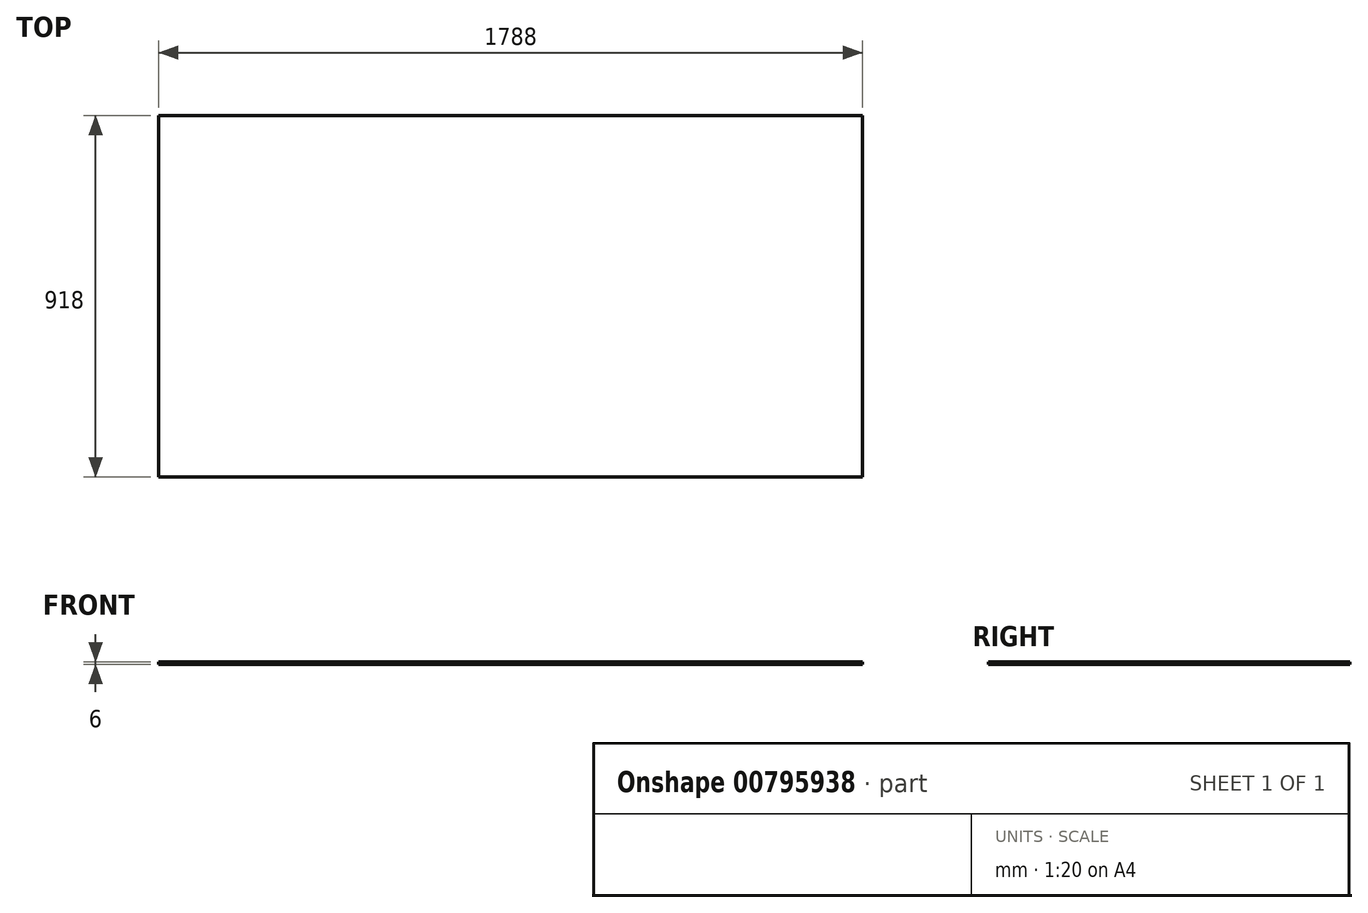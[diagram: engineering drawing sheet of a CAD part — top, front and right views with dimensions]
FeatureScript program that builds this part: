
annotation { "Feature Type Name" : "Feature", "Feature Type Description" : "" }
export const myFeature = defineFeature(function(context is Context, id is Id, definition is map)
    precondition{}
    {
        {
            var Q0;
            Q0=qCreatedBy(makeId("Top.planeOp"),FACE);
            var sketch = newSketch(context, id + "F0", { "sketchPlane" : qUnion([Q0])});
            skLineSegment(sketch, "E0.bottom", {"start": v(894, 459) * mm, "end": v(-894, 459) * mm});
            skLineSegment(sketch, "E0.top", {"start": v(894, -459) * mm, "end": v(-894, -459) * mm});
            skLineSegment(sketch, "E0.left", {"start": v(894, 459) * mm, "end": v(894, -459) * mm});
            skLineSegment(sketch, "E0.right", {"start": v(-894, 459) * mm, "end": v(-894, -459) * mm});
            skPoint(sketch, "E0.middle", {"position": v(0, 0) * mm});
            skSolve(sketch);
        }
        {
            var Q0;
            Q0 = qSketchRegion(id + "F0", true);
            extrude(context, id + "F1", {"entities" : qUnion([Q0]), "depth" : 6 * mm, "offsetDistance" : 25 * mm});
        }
    });
